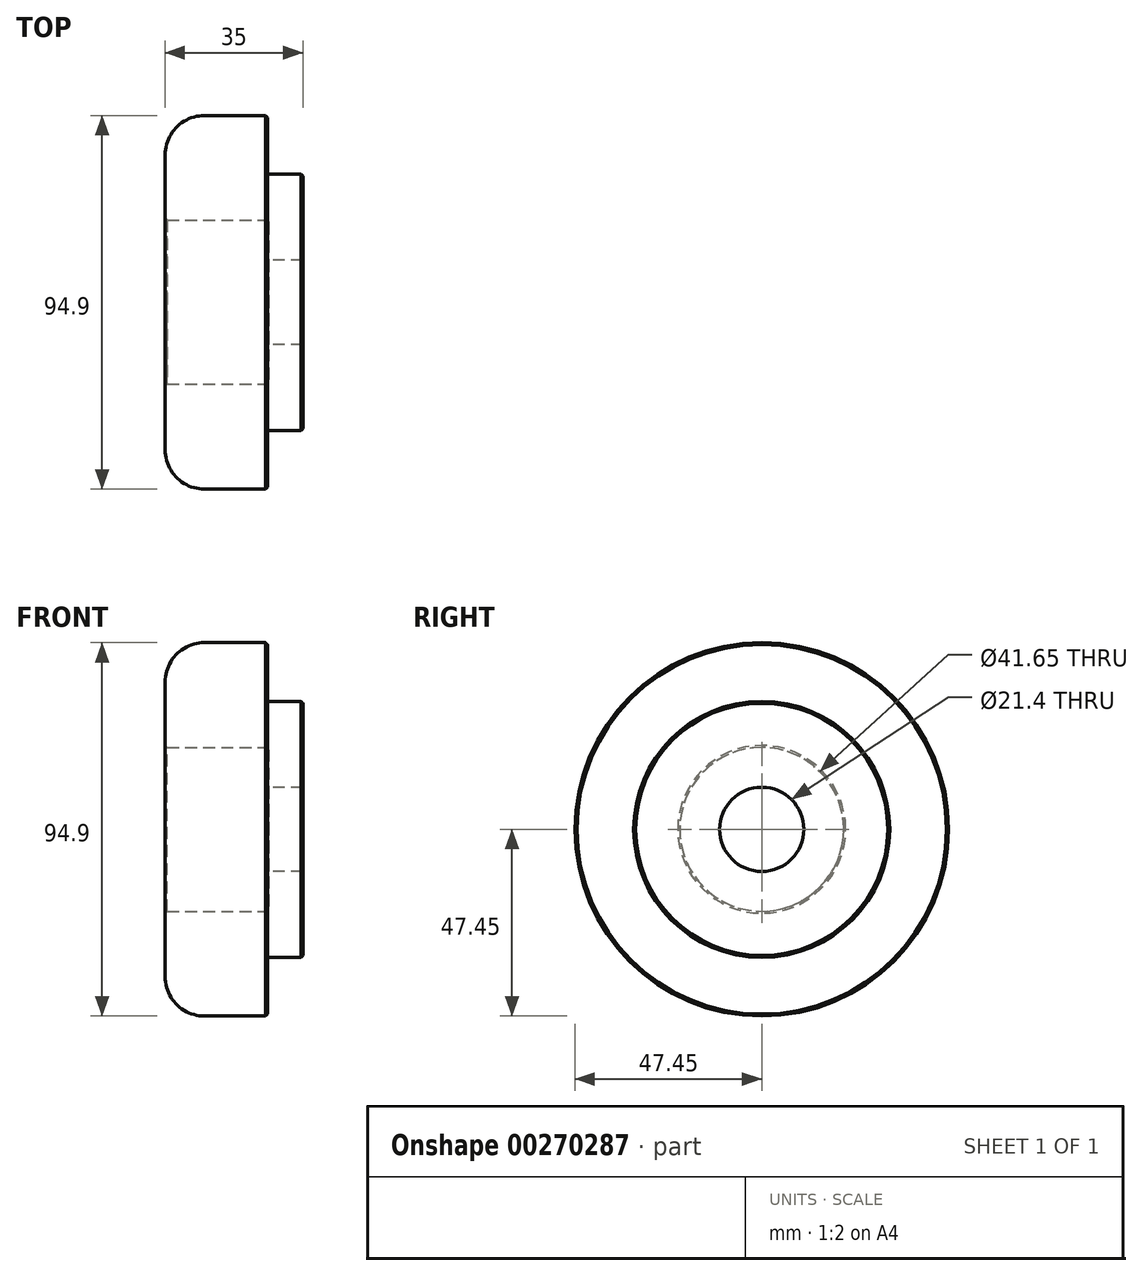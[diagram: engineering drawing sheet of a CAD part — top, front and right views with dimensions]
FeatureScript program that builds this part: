
annotation { "Feature Type Name" : "Feature", "Feature Type Description" : "" }
export const myFeature = defineFeature(function(context is Context, id is Id, definition is map)
    precondition{}
    {
        {
            var Q0;
            Q0=qCreatedBy(makeId("Front.planeOp"),FACE);
            var sketch = newSketch(context, id + "F0", { "sketchPlane" : qUnion([Q0])});
            skLineSegment(sketch, "E0", {"start": v(0, 0) * mm, "end": v(-8.7, 0) * mm});
            skLineSegment(sketch, "E1", {"start": v(-35, 20.82) * mm, "end": v(-35, 47.45) * mm});
            skLineSegment(sketch, "E2", {"start": v(-35, 47.45) * mm, "end": v(-9, 47.45) * mm});
            skLineSegment(sketch, "E3", {"start": v(-9, 47.45) * mm, "end": v(-9, 32.53) * mm});
            skLineSegment(sketch, "E4", {"start": v(-9, 32.53) * mm, "end": v(0, 32.53) * mm});
            skLineSegment(sketch, "E5", {"start": v(0, 32.53) * mm, "end": v(0, 0) * mm});
            skLineSegment(sketch, "E6", {"start": v(-35, 20.82) * mm, "end": v(-8.7, 20.83) * mm});
            skLineSegment(sketch, "E7", {"start": v(-8.7, 20.82) * mm, "end": v(-8.7, 0) * mm});
            skSolve(sketch);
        }
        {
            var Q0;
            Q0 = qSketchRegion(id + "F0", true);
            var Q1;
            Q1=sQuery(id+"F0.wireOp",EDGE,"E0");
            revolve(context, id + "F1", {"entities" : qUnion([Q0]), "axis" : qUnion([Q1]), "revolveType" : RevolveType.FULL});
        }
        {
            var Q0;
            Q0=makeQuery(id+"F1.opRevolve","SWEPT_EDGE",EDGE,{"disambiguationData":[OSD([sQuery(id+"F0.wireOp",EDGE,"E1"),sQuery(id+"F0.wireOp",EDGE,"E2")])]});
            fillet(context, id + "F2", {"entities" : qUnion([Q0]), "radius" : 10 * mm, "tangentPropagation" : true, "allowEdgeOverflow" : false});
        }
        {
            var Q0;
            Q0=makeQuery(id+"F1.opRevolve","SWEPT_FACE",FACE,{"disambiguationData":[OSD([sQuery(id+"F0.wireOp",EDGE,"E7")])]});
            var sketch = newSketch(context, id + "F3", { "sketchPlane" : qUnion([Q0])});
            skCircle(sketch, "E8", {"center": v(0, 0) * mm, "radius": 10.7 * mm});
            skSolve(sketch);
        }
        {
            var Q0;
            Q0 = qSketchRegion(id + "F3", true);
            var Q1;
            Q1=makeQuery(id+"F1.opRevolve","SWEPT_FACE",FACE,{"disambiguationData":[OSD([sQuery(id+"F0.wireOp",EDGE,"E5")])]});
            extrude(context, id + "F4", {"entities" : qUnion([Q0]), "operationType" : NewBodyOperationType.REMOVE, "endBound" : BoundingType.UP_TO_SURFACE, "oppositeDirection" : true, "endBoundEntityFace" : qUnion([Q1]), "depth" : 25 * mm});
        }
        {
            var Q0;
            Q0=makeQuery(id+"F1.opRevolve","SWEPT_EDGE",EDGE,{"disambiguationData":[OSD([sQuery(id+"F0.wireOp",EDGE,"E6"),sQuery(id+"F0.wireOp",EDGE,"E7")])]});
            var Q1;
            Q1=makeQuery(id+"F1.opRevolve","SWEPT_EDGE",EDGE,{"disambiguationData":[OSD([sQuery(id+"F0.wireOp",EDGE,"E3"),sQuery(id+"F0.wireOp",EDGE,"E4")])]});
            fillet(context, id + "F5", {"entities" : qUnion([Q0, Q1]), "radius" : .6 * mm, "tangentPropagation" : true, "allowEdgeOverflow" : false});
        }
        {
            var Q0;
            Q0=makeQuery(id+"F1.opRevolve","SWEPT_EDGE",EDGE,{"disambiguationData":[OSD([sQuery(id+"F0.wireOp",EDGE,"E2"),sQuery(id+"F0.wireOp",EDGE,"E3")])]});
            var Q1;
            Q1=makeQuery(id+"F1.opRevolve","SWEPT_EDGE",EDGE,{"disambiguationData":[OSD([sQuery(id+"F0.wireOp",EDGE,"E4"),sQuery(id+"F0.wireOp",EDGE,"E5")])]});
            var Q2;
            Q2=makeQuery(id+"F4.boolean.opBoolean","COPY",EDGE,{"derivedFrom":makeQuery(id+"F4.opExtrude","CAP_EDGE",EDGE,{"disambiguationData":[OSD([sQuery(id+"F3.wireOp",EDGE,"E8")])],"isStart":false})});
            var Q3;
            Q3=makeQuery(id+"F4.boolean.opBoolean","COPY",EDGE,{"derivedFrom":makeQuery(id+"F4.opExtrude","CAP_EDGE",EDGE,{"disambiguationData":[OSD([sQuery(id+"F3.wireOp",EDGE,"E8")])],"isStart":true})});
            var Q4;
            Q4=makeQuery(id+"F1.opRevolve","SWEPT_EDGE",EDGE,{"disambiguationData":[OSD([sQuery(id+"F0.wireOp",EDGE,"E1"),sQuery(id+"F0.wireOp",EDGE,"E6")])]});
            chamfer(context, id + "F6", {"entities" : qUnion([Q0, Q1, Q2, Q3, Q4]), "width" : .5 * mm, "tangentPropagation" : true});
        }
    });
